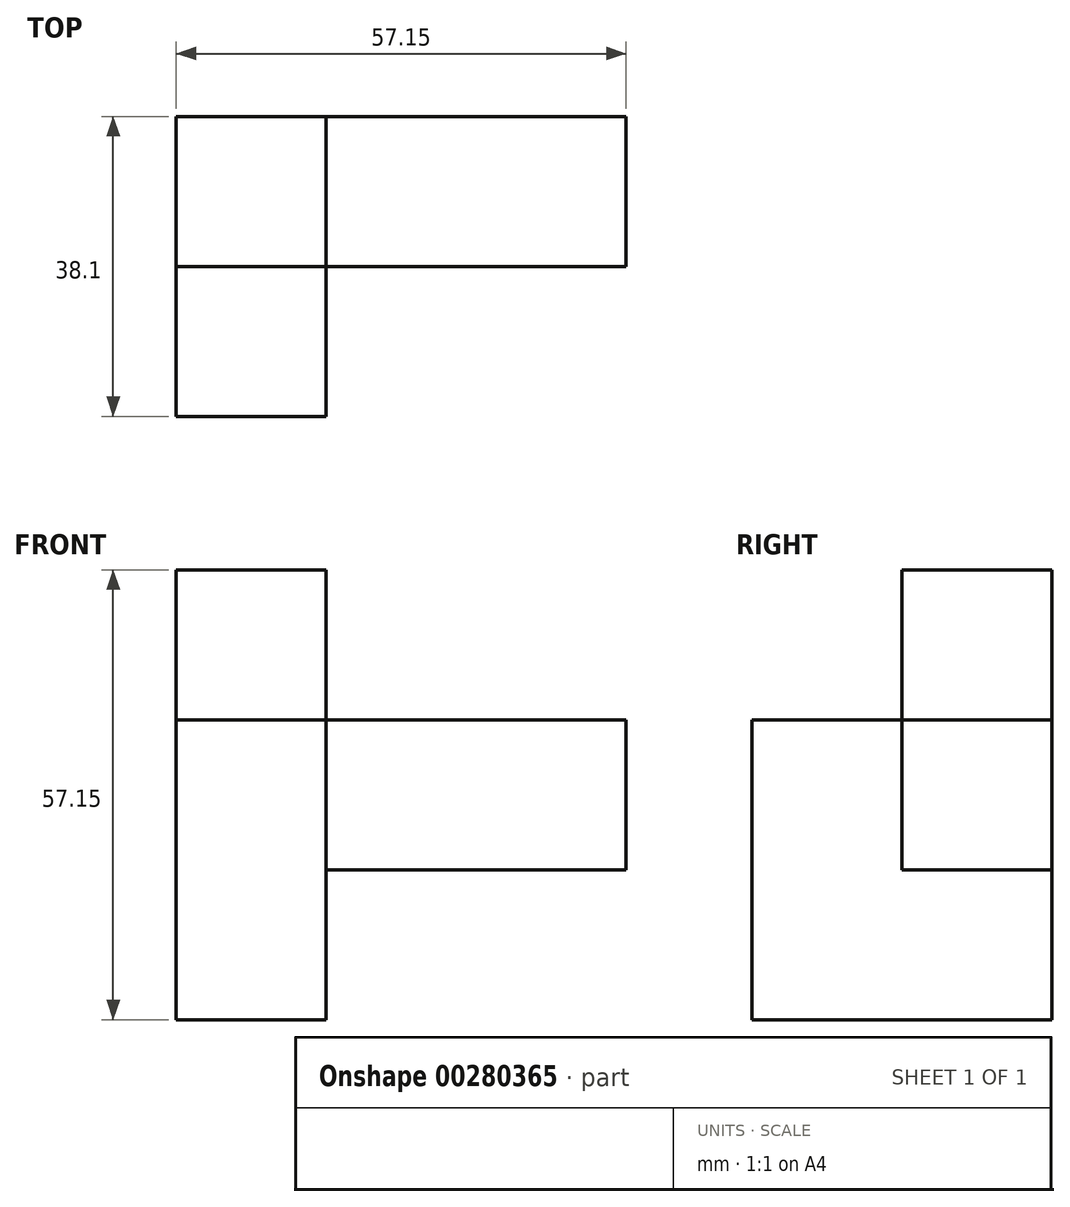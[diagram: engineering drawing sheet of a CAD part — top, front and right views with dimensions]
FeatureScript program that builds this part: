
annotation { "Feature Type Name" : "Feature", "Feature Type Description" : "" }
export const myFeature = defineFeature(function(context is Context, id is Id, definition is map)
    precondition{}
    {
        {
            var Q0;
            Q0=qCreatedBy(makeId("Top.planeOp"),FACE);
            var sketch = newSketch(context, id + "F0", { "sketchPlane" : qUnion([Q0])});
            skLineSegment(sketch, "E0.bottom", {"start": v(0, 0) * mm, "end": v(19.05, 0) * mm});
            skLineSegment(sketch, "E0.top", {"start": v(0, 38.1) * mm, "end": v(19.05, 38.1) * mm});
            skLineSegment(sketch, "E0.left", {"start": v(0, 0) * mm, "end": v(0, 38.1) * mm});
            skLineSegment(sketch, "E0.right", {"start": v(19.05, 0) * mm, "end": v(19.05, 38.1) * mm});
            skLineSegment(sketch, "E1.bottom", {"start": v(19.05, 0) * mm, "end": v(0, 0) * mm});
            skLineSegment(sketch, "E1.top", {"start": v(19.05, 38.1) * mm, "end": v(0, 38.1) * mm});
            skSolve(sketch);
        }
        {
            var Q0;
            Q0 = qSketchRegion(id + "F0", true);
            extrude(context, id + "F1", {"entities" : qUnion([Q0]), "depth" : 57.15 * mm});
        }
        {
            var Q0;
            Q0=makeQuery(id+"F1.opExtrude","SWEPT_FACE",FACE,{"disambiguationData":[OSD([sQuery(id+"F0.wireOp",EDGE,"E0.right")])]});
            var sketch = newSketch(context, id + "F2", { "sketchPlane" : qUnion([Q0])});
            skLineSegment(sketch, "E2.bottom", {"start": v(0, 57.15) * mm, "end": v(19.05, 57.15) * mm});
            skLineSegment(sketch, "E2.top", {"start": v(0, 38.1) * mm, "end": v(19.05, 38.1) * mm});
            skLineSegment(sketch, "E2.left", {"start": v(0, 57.15) * mm, "end": v(0, 38.1) * mm});
            skLineSegment(sketch, "E2.right", {"start": v(19.05, 57.15) * mm, "end": v(19.05, 38.1) * mm});
            skSolve(sketch);
        }
        {
            var Q0;
            Q0 = qSketchRegion(id + "F2", true);
            extrude(context, id + "F3", {"entities" : qUnion([Q0]), "operationType" : NewBodyOperationType.REMOVE, "oppositeDirection" : true, "depth" : 19.05 * mm});
        }
        {
            var Q0;
            Q0=makeQuery(id+"F1.opExtrude","SWEPT_FACE",FACE,{"disambiguationData":[OSD([sQuery(id+"F0.wireOp",EDGE,"E0.right")])]});
            var sketch = newSketch(context, id + "F4", { "sketchPlane" : qUnion([Q0])});
            skLineSegment(sketch, "E3.bottom", {"start": v(19.05, 38.1) * mm, "end": v(38.1, 38.1) * mm});
            skLineSegment(sketch, "E3.top", {"start": v(19.05, 19.05) * mm, "end": v(38.1, 19.05) * mm});
            skLineSegment(sketch, "E3.left", {"start": v(19.05, 38.1) * mm, "end": v(19.05, 19.05) * mm});
            skLineSegment(sketch, "E3.right", {"start": v(38.1, 38.1) * mm, "end": v(38.1, 19.05) * mm});
            skSolve(sketch);
        }
        {
            var Q0;
            Q0 = qSketchRegion(id + "F4", true);
            extrude(context, id + "F5", {"entities" : qUnion([Q0]), "operationType" : NewBodyOperationType.ADD, "depth" : 38.1 * mm});
        }
    });
